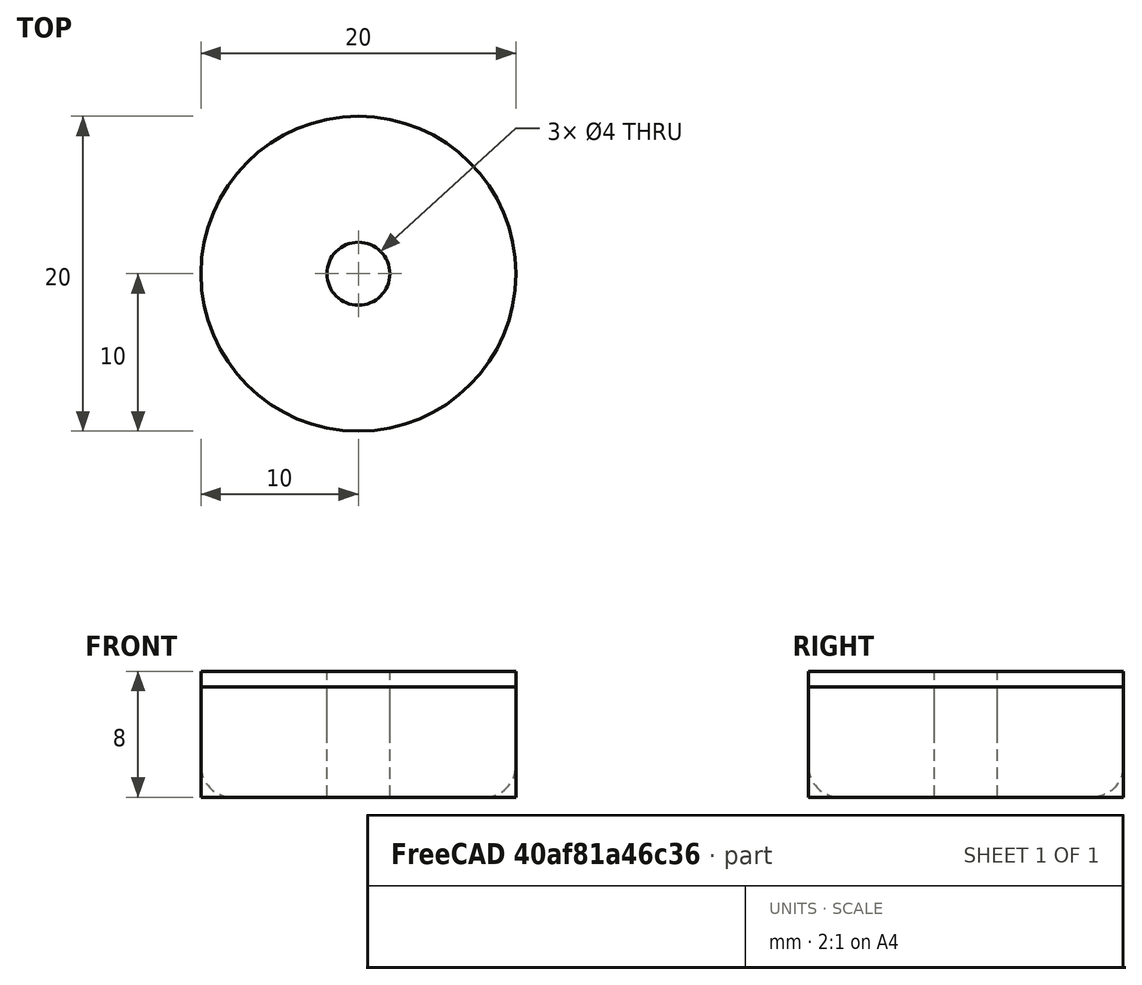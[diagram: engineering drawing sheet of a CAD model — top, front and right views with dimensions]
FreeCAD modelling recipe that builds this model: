
FCSTD DOCUMENT  (FreeCAD 0.19R)
Label: leg
License: All rights reserved
LicenseURL: http://en.wikipedia.org/wiki/All_rights_reserved
objects: Part::Cylinder×3, App::Part×2, Part::Fillet×1, Part::MultiFuse×1, Part::Cut×1, Part::FeaturePython×1
note: 7 computed .brp shape members not serialized (recipe doc carries the construction recipe); baked Part::Feature solids carry a one-line shape summary decoded from their .brp

FEATURE [Part::Cylinder] Cylinder  label="external"
  Angle = 360
  AttacherType = Attacher::AttachEngine3D
  Height = 8
  Radius = 10
FEATURE [Part::Cylinder] Cylinder001  label="bolt hole"
  Angle = 360
  AttacherType = Attacher::AttachEngine3D
  Height = 30
  Radius = 2
FEATURE [Part::Fillet] Fillet
  Base = -> Cylinder
  Edges = 1 edges r=2: [Edge3]
FEATURE [Part::Cylinder] Cylinder002  label="bolt head hole"
  Angle = 360
  AttacherType = Attacher::AttachEngine3D
  Height = 4
  Radius = 2
  expr: Height = <<external>>.Height - 4mm
FEATURE [Part::MultiFuse] Fusion  label="hole fusion"
  Shapes = -> [Cylinder002,Cylinder001]
FEATURE [Part::Cut] Cut  label="leg cut"
  Base = -> Fillet
  Tool = -> Fusion
FEATURE [App::Part] Part  label="leg"
  Group = -> [Cut]
  Origin = -> Origin
FEATURE [Part::FeaturePython] Tube  # WARN: FeaturePython — macro-defined, semantics opaque (R4)
  AttacherType = Attacher::AttachEngine3D
  Height = 5
  InnerRadius = 2
  OuterRadius = 10
  expr: InnerRadius = <<bolt head hole>>.Radius
  expr: OuterRadius = <<external>>.Radius
FEATURE [App::Part] Part001  label="big washer"
  Group = -> [Tube]
  Origin = -> Origin001
